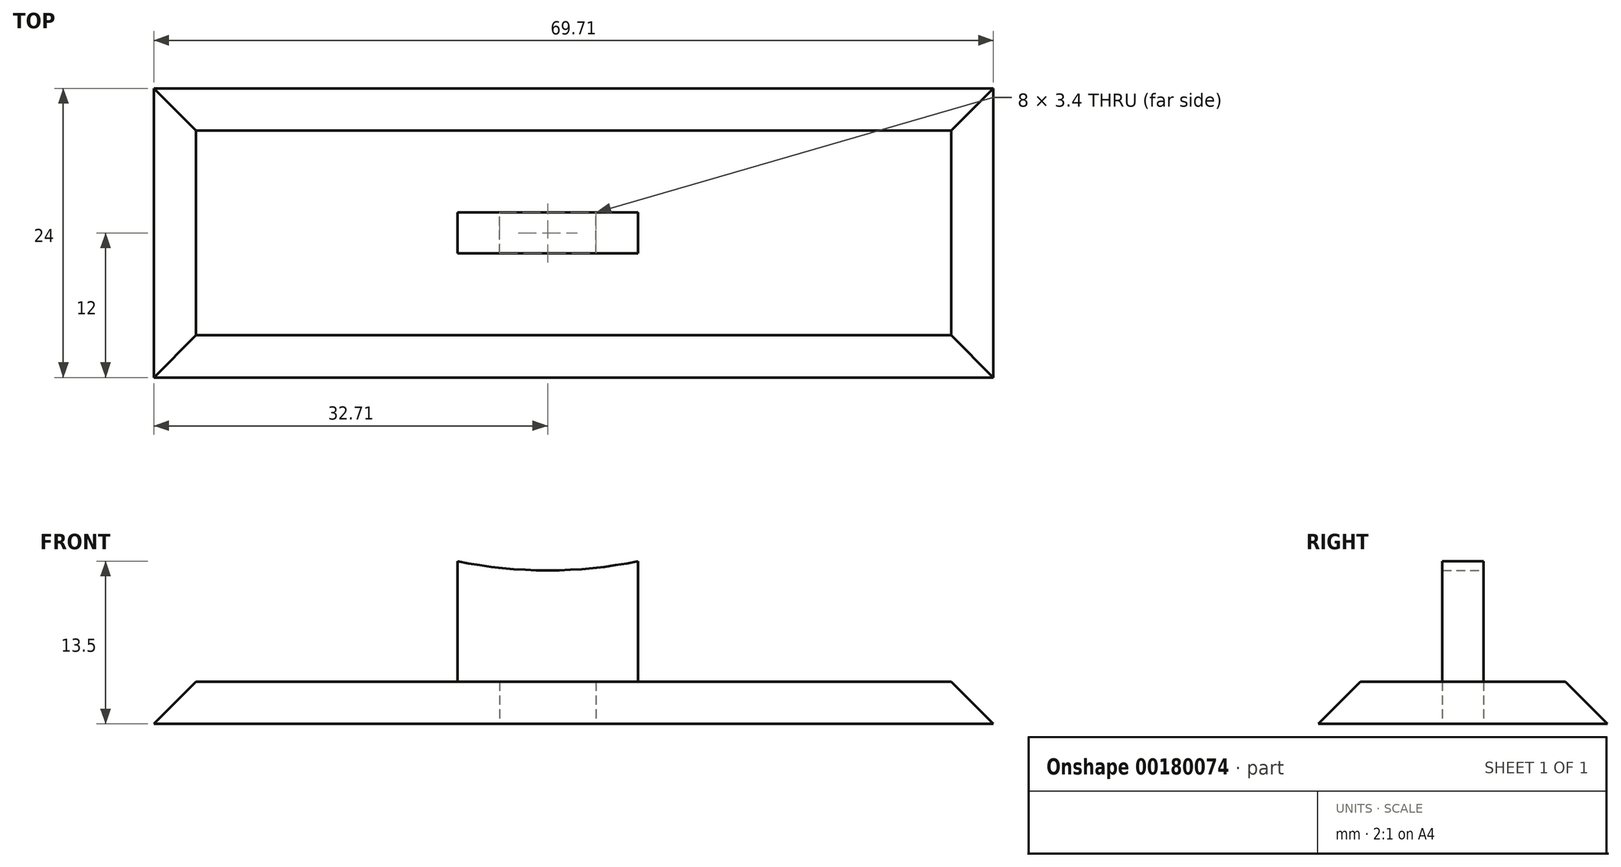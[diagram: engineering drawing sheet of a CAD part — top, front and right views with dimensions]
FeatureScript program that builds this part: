
annotation { "Feature Type Name" : "Feature", "Feature Type Description" : "" }
export const myFeature = defineFeature(function(context is Context, id is Id, definition is map)
    precondition{}
    {
        {
            var Q0;
            Q0=qCreatedBy(makeId("Top.planeOp"),FACE);
            var sketch = newSketch(context, id + "F0", { "sketchPlane" : qUnion([Q0])});
            skLineSegment(sketch, "E0.bottom", {"start": v(-33.2, 12.5) * mm, "end": v(37.5, 12.5) * mm});
            skLineSegment(sketch, "E0.top", {"start": v(-33.2, -12.5) * mm, "end": v(37.5, -12.5) * mm});
            skLineSegment(sketch, "E0.left", {"start": v(-33.2, 12.5) * mm, "end": v(-33.2, -12.5) * mm});
            skLineSegment(sketch, "E0.right", {"start": v(37.5, 12.5) * mm, "end": v(37.5, -12.5) * mm});
            skSolve(sketch);
        }
        {
            var Q0;
            Q0 = qSketchRegion(id + "F0", true);
            extrude(context, id + "F1", {"entities" : qUnion([Q0]), "depth" : 3.5 * mm});
        }
        {
            var Q0;
            Q0=makeQuery(id+"F1.opExtrude","CAP_EDGE",EDGE,{"disambiguationData":[OSD([sQuery(id+"F0.wireOp",EDGE,"E0.top")])],"isStart":false});
            var Q1;
            Q1=makeQuery(id+"F1.opExtrude","CAP_EDGE",EDGE,{"disambiguationData":[OSD([sQuery(id+"F0.wireOp",EDGE,"E0.left")])],"isStart":false});
            var Q2;
            Q2=makeQuery(id+"F1.opExtrude","CAP_EDGE",EDGE,{"disambiguationData":[OSD([sQuery(id+"F0.wireOp",EDGE,"E0.bottom")])],"isStart":false});
            var Q3;
            Q3=makeQuery(id+"F1.opExtrude","CAP_EDGE",EDGE,{"disambiguationData":[OSD([sQuery(id+"F0.wireOp",EDGE,"E0.right")])],"isStart":false});
            chamfer(context, id + "F2", {"entities" : qUnion([Q0, Q1, Q2, Q3]), "width" : 4 * mm, "tangentPropagation" : true});
        }
        {
            var Q0;
            Q0=qCreatedBy(makeId("Top.planeOp"),FACE);
            var sketch = newSketch(context, id + "F3", { "sketchPlane" : qUnion([Q0])});
            skLineSegment(sketch, "E1.bottom", {"start": v(-4, -1.7) * mm, "end": v(4, -1.7) * mm});
            skLineSegment(sketch, "E1.top", {"start": v(-4, 1.7) * mm, "end": v(4, 1.7) * mm});
            skLineSegment(sketch, "E1.left", {"start": v(-4, -1.7) * mm, "end": v(-4, 1.7) * mm});
            skLineSegment(sketch, "E1.right", {"start": v(4, -1.7) * mm, "end": v(4, 1.7) * mm});
            skSolve(sketch);
        }
        {
            var Q0;
            Q0 = qSketchRegion(id + "F3", true);
            extrude(context, id + "F4", {"entities" : qUnion([Q0]), "operationType" : NewBodyOperationType.REMOVE, "depth" : 3.5 * mm});
        }
        {
            var Q0;
            Q0=qCreatedBy(makeId("Front.planeOp"),FACE);
            var sketch = newSketch(context, id + "F5", { "sketchPlane" : qUnion([Q0])});
            skLineSegment(sketch, "E2", {"start": v(-4, 0) * mm, "end": v(-4, 3.5) * mm});
            skLineSegment(sketch, "E3", {"start": v(-7.5, 3.5) * mm, "end": v(-7.5, 13.5) * mm});
            skLineSegment(sketch, "E4", {"start": v(4, 0) * mm, "end": v(4, 3.5) * mm});
            skLineSegment(sketch, "E5", {"start": v(4, 3.5) * mm, "end": v(7.5, 3.5) * mm});
            skLineSegment(sketch, "E6", {"start": v(7.5, 3.5) * mm, "end": v(7.5, 13.5) * mm});
            skLineSegment(sketch, "E7", {"start": v(-4, 0) * mm, "end": v(4, 0) * mm});
            skArc(sketch, "E8", {"start": v(-7.5, 13.5) * mm, "mid": v(0, 12.74) * mm, "end": v(7.5, 13.5) * mm});
            skLineSegment(sketch, "E9", {"start": v(-7.5, 3.5) * mm, "end": v(-4, 3.5) * mm});
            skSolve(sketch);
        }
        {
            var Q0;
            Q0=makeQuery(id+"F5.imprint","IMPRINT",FACE,{"disambiguationData":[TD([[makeQuery(id+"F5.imprint","IMPRINT",EDGE,{"derivedFrom":sQuery(id+"F5.wireOp",EDGE,"E2")}),-1.0]])]});
            extrude(context, id + "F6", {"entities" : qUnion([Q0]), "endBound" : BoundingType.SYMMETRIC, "depth" : 3.4 * mm});
        }
    });
